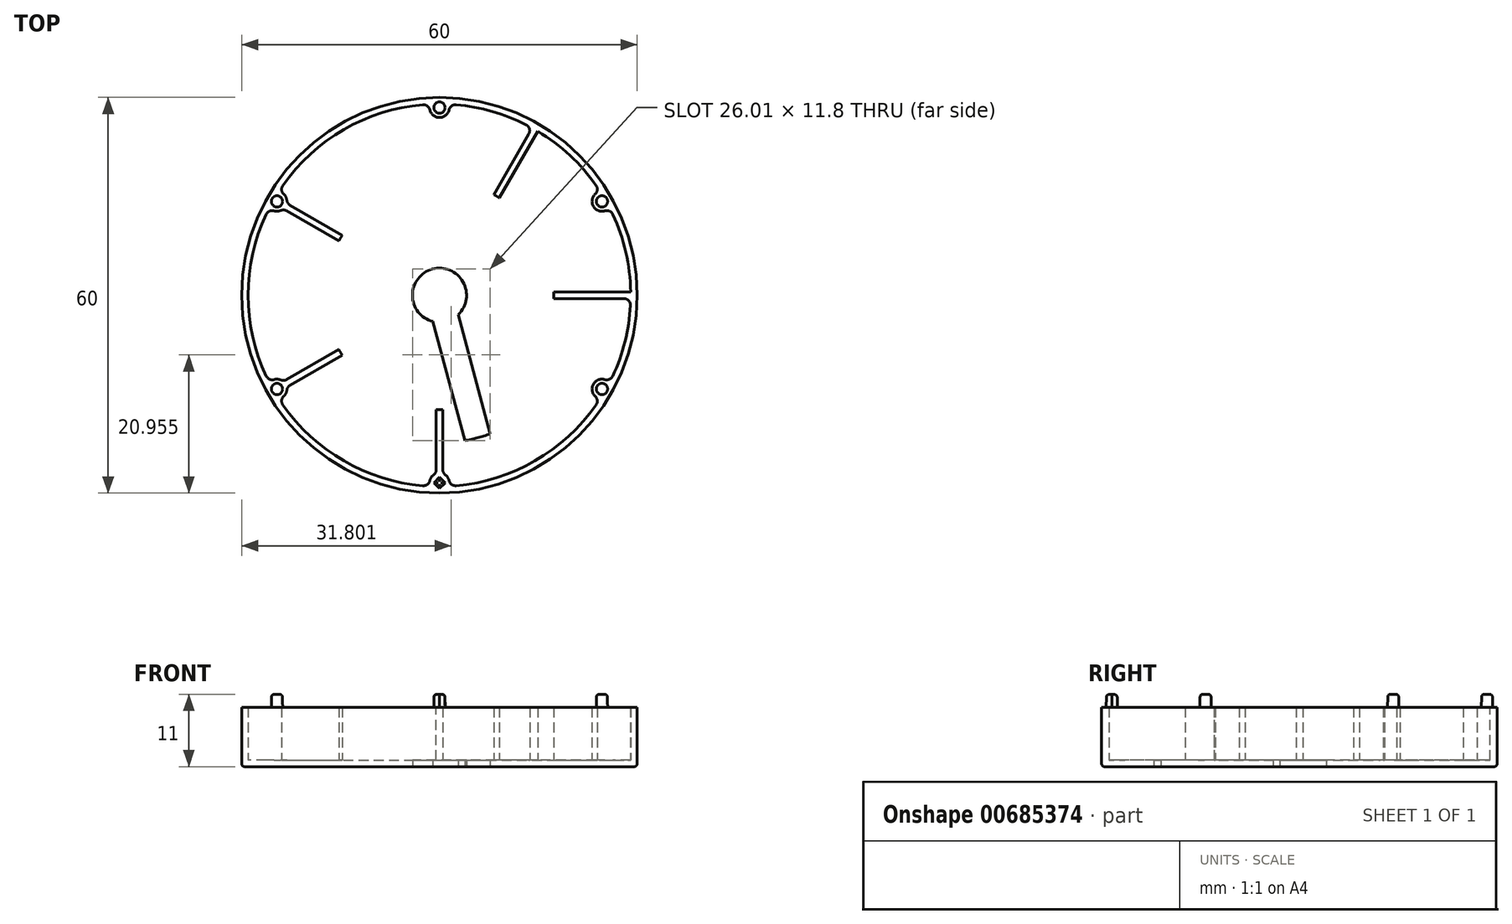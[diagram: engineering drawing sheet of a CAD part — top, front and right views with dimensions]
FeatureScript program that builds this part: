
annotation { "Feature Type Name" : "Feature", "Feature Type Description" : "" }
export const myFeature = defineFeature(function(context is Context, id is Id, definition is map)
    precondition{}
    {
        {
            var Q0;
            Q0=qCreatedBy(makeId("Top.planeOp"),FACE);
            var sketch = newSketch(context, id + "F0", { "sketchPlane" : qUnion([Q0])});
            skCircle(sketch, "E0", {"center": v(0, 0) * mm, "radius": 30 * mm});
            skCircle(sketch, "E1.0", {"center": v(0, 0) * mm, "radius": 29 * mm});
            skLineSegment(sketch, "E2.bottom", {"start": v(14.56, 26.23) * mm, "end": v(15.43, 25.73) * mm});
            skLineSegment(sketch, "E2.top", {"start": v(-15.43, -25.73) * mm, "end": v(-14.56, -26.23) * mm});
            skLineSegment(sketch, "E2.left", {"start": v(14.56, 26.23) * mm, "end": v(-15.43, -25.73) * mm});
            skLineSegment(sketch, "E2.right", {"start": v(15.43, 25.73) * mm, "end": v(-14.56, -26.23) * mm});
            skLineSegment(sketch, "E3.bottom", {"start": v(25.73, 15.43) * mm, "end": v(26.23, 14.56) * mm});
            skLineSegment(sketch, "E3.top", {"start": v(-26.23, -14.56) * mm, "end": v(-25.73, -15.43) * mm});
            skLineSegment(sketch, "E3.left", {"start": v(25.73, 15.43) * mm, "end": v(-26.23, -14.56) * mm});
            skLineSegment(sketch, "E3.right", {"start": v(26.23, 14.56) * mm, "end": v(-25.73, -15.43) * mm});
            skLineSegment(sketch, "E4", {"start": v(-38.35, 0) * mm, "end": v(39.17, 0) * mm, "construction": true});
            skLineSegment(sketch, "E5", {"start": v(0, 42.5) * mm, "end": v(0, -42.47) * mm, "construction": true});
            skLineSegment(sketch, "E6.bottom", {"start": v(-30, 0.5) * mm, "end": v(30, 0.5) * mm});
            skLineSegment(sketch, "E6.top", {"start": v(-30, -0.5) * mm, "end": v(30, -0.5) * mm});
            skLineSegment(sketch, "E6.left", {"start": v(-30, 0.5) * mm, "end": v(-30, -0.5) * mm});
            skLineSegment(sketch, "E6.right", {"start": v(30, 0.5) * mm, "end": v(30, -0.5) * mm});
            skLineSegment(sketch, "E7.bottom", {"start": v(-25.73, 15.43) * mm, "end": v(26.23, -14.56) * mm});
            skLineSegment(sketch, "E7.top", {"start": v(-26.23, 14.56) * mm, "end": v(25.73, -15.43) * mm});
            skLineSegment(sketch, "E7.left", {"start": v(-25.73, 15.43) * mm, "end": v(-26.23, 14.56) * mm});
            skLineSegment(sketch, "E7.right", {"start": v(26.23, -14.56) * mm, "end": v(25.73, -15.43) * mm});
            skLineSegment(sketch, "E8.bottom", {"start": v(-0.5, 30) * mm, "end": v(0.5, 30) * mm});
            skLineSegment(sketch, "E8.top", {"start": v(-0.5, -30) * mm, "end": v(0.5, -30) * mm});
            skLineSegment(sketch, "E8.left", {"start": v(-0.5, 30) * mm, "end": v(-0.5, -30) * mm});
            skLineSegment(sketch, "E8.right", {"start": v(0.5, 30) * mm, "end": v(0.5, -30) * mm});
            skLineSegment(sketch, "E9.bottom", {"start": v(-15.43, 25.73) * mm, "end": v(-14.56, 26.23) * mm});
            skLineSegment(sketch, "E9.top", {"start": v(14.56, -26.23) * mm, "end": v(15.43, -25.73) * mm});
            skLineSegment(sketch, "E9.left", {"start": v(-15.43, 25.73) * mm, "end": v(14.56, -26.23) * mm});
            skLineSegment(sketch, "E9.right", {"start": v(-14.56, 26.23) * mm, "end": v(15.43, -25.73) * mm});
            skCircle(sketch, "E10", {"center": v(0, 0) * mm, "radius": 17.33 * mm});
            skSolve(sketch);
        }
        {
            var Q0;
            Q0=qCreatedBy(makeId("Top.planeOp"),FACE);
            var sketch = newSketch(context, id + "F1", { "sketchPlane" : qUnion([Q0])});
            skCircle(sketch, "E11", {"center": v(0, 0) * mm, "radius": 30 * mm});
            skCircle(sketch, "E12", {"center": v(0, 0) * mm, "radius": 29 * mm});
            skSolve(sketch);
        }
        {
            var Q0;
            Q0=makeQuery(id+"F1.imprint","IMPRINT",FACE,{"disambiguationData":[TD([[makeQuery(id+"F1.imprint","IMPRINT",EDGE,{"derivedFrom":sQuery(id+"F1.wireOp",EDGE,"E11")}),1.0]])]});
            extrude(context, id + "F2", {"entities" : qUnion([Q0]), "depth" : 9 * mm, "offsetDistance" : 25 * mm});
        }
        {
            var Q0;
            Q0=qSketchRegion(id+"F1",true);
            var Q1;
            {var subQ0=sQuery(id+"F0.wireOp",EDGE,"E7.bottom");var subQ1=sQuery(id+"F0.wireOp",EDGE,"E1.0");var subQ2=makeQuery(id+"F0.imprint","INTERSECT",VERTEX,{"disambiguationData":[OD(0.0)],"derivedFrom":[subQ1,subQ0]});Q1=makeQuery(id+"F0.imprint","IMPRINT",FACE,{"disambiguationData":[TD([[makeQuery(id+"F0.imprint","IMPRINT",EDGE,{"disambiguationData":[TD([[subQ2,-1.0]])],"derivedFrom":subQ1}),1.0]])]});}
            var Q2;
            {var subQ0=sQuery(id+"F0.wireOp",EDGE,"E2.right");var subQ1=sQuery(id+"F0.wireOp",EDGE,"E1.0");var subQ2=makeQuery(id+"F0.imprint","INTERSECT",VERTEX,{"disambiguationData":[OD(0.0)],"derivedFrom":[subQ1,subQ0]});Q2=makeQuery(id+"F0.imprint","IMPRINT",FACE,{"disambiguationData":[TD([[makeQuery(id+"F0.imprint","IMPRINT",EDGE,{"disambiguationData":[TD([[subQ2,-1.0]])],"derivedFrom":subQ1}),1.0]])]});}
            var Q3;
            {var subQ0=sQuery(id+"F0.wireOp",EDGE,"E6.bottom");var subQ1=sQuery(id+"F0.wireOp",EDGE,"E1.0");var subQ2=makeQuery(id+"F0.imprint","INTERSECT",VERTEX,{"disambiguationData":[OD(0.0)],"derivedFrom":[subQ1,subQ0]});Q3=makeQuery(id+"F0.imprint","IMPRINT",FACE,{"disambiguationData":[TD([[makeQuery(id+"F0.imprint","IMPRINT",EDGE,{"disambiguationData":[TD([[subQ2,1.0]])],"derivedFrom":subQ1}),1.0]])]});}
            var Q4;
            {var subQ0=sQuery(id+"F0.wireOp",EDGE,"E8.left");var subQ1=sQuery(id+"F0.wireOp",EDGE,"E1.0");var subQ2=makeQuery(id+"F0.imprint","INTERSECT",VERTEX,{"disambiguationData":[OD(1.0)],"derivedFrom":[subQ1,subQ0]});Q4=makeQuery(id+"F0.imprint","IMPRINT",FACE,{"disambiguationData":[TD([[makeQuery(id+"F0.imprint","IMPRINT",EDGE,{"disambiguationData":[TD([[subQ2,-1.0]])],"derivedFrom":subQ1}),1.0]])]});}
            var Q5;
            {var subQ0=sQuery(id+"F0.wireOp",EDGE,"E3.left");var subQ1=sQuery(id+"F0.wireOp",EDGE,"E1.0");var subQ2=makeQuery(id+"F0.imprint","INTERSECT",VERTEX,{"disambiguationData":[OD(1.0)],"derivedFrom":[subQ1,subQ0]});Q5=makeQuery(id+"F0.imprint","IMPRINT",FACE,{"disambiguationData":[TD([[makeQuery(id+"F0.imprint","IMPRINT",EDGE,{"disambiguationData":[TD([[subQ2,-1.0]])],"derivedFrom":subQ1}),1.0]])]});}
            extrude(context, id + "F3", {"entities" : qUnion([Q0, Q1, Q2, Q3, Q4, Q5]), "operationType" : NewBodyOperationType.ADD, "depth" : 9 * mm, "offsetDistance" : 25 * mm});
        }
        {
            var Q0;
            Q0=makeQuery(id+"F1.imprint","IMPRINT",FACE,{"disambiguationData":[TD([[makeQuery(id+"F1.imprint","IMPRINT",EDGE,{"derivedFrom":sQuery(id+"F1.wireOp",EDGE,"E11")}),1.0]])]});
            var Q1;
            Q1=makeQuery(id+"F1.imprint","IMPRINT",FACE,{"disambiguationData":[TD([[makeQuery(id+"F1.imprint","IMPRINT",EDGE,{"derivedFrom":sQuery(id+"F1.wireOp",EDGE,"E12")}),1.0]])]});
            extrude(context, id + "F4", {"entities" : qUnion([Q0, Q1]), "operationType" : NewBodyOperationType.ADD, "depth" : 1 * mm, "offsetDistance" : 25 * mm});
        }
        {
            var Q0;
            Q0=qCreatedBy(makeId("Top.planeOp"),FACE);
            var sketch = newSketch(context, id + "F5", { "sketchPlane" : qUnion([Q0])});
            skCircle(sketch, "E13", {"center": v(0, 0) * mm, "radius": 28.45 * mm});
            skLineSegment(sketch, "E14", {"start": v(0, 28.45) * mm, "end": v(0, -28.45) * mm, "construction": true});
            skLineSegment(sketch, "E15", {"start": v(24.64, 14.22) * mm, "end": v(0, 0) * mm, "construction": true});
            skLineSegment(sketch, "E16", {"start": v(14.23, 24.64) * mm, "end": v(0, 0) * mm, "construction": true});
            skLineSegment(sketch, "E17", {"start": v(0, 0) * mm, "end": v(28.45, 0) * mm, "construction": true});
            skLineSegment(sketch, "E18", {"start": v(0, 0) * mm, "end": v(24.64, -14.22) * mm, "construction": true});
            skLineSegment(sketch, "E19", {"start": v(0, 0) * mm, "end": v(14.23, -24.64) * mm, "construction": true});
            skLineSegment(sketch, "E20", {"start": v(0, 0) * mm, "end": v(-14.23, 24.64) * mm, "construction": true});
            skLineSegment(sketch, "E21", {"start": v(0, 0) * mm, "end": v(-24.64, 14.22) * mm, "construction": true});
            skLineSegment(sketch, "E22", {"start": v(0, 0) * mm, "end": v(-28.45, 0) * mm, "construction": true});
            skLineSegment(sketch, "E23", {"start": v(0, 0) * mm, "end": v(-24.64, -14.23) * mm, "construction": true});
            skLineSegment(sketch, "E24", {"start": v(0, 0) * mm, "end": v(-14.22, -24.64) * mm, "construction": true});
            skCircle(sketch, "E25", {"center": v(0, 28.45) * mm, "radius": 1.5 * mm});
            skCircle(sketch, "E26", {"center": v(24.64, 14.22) * mm, "radius": 1.5 * mm});
            skCircle(sketch, "E27", {"center": v(24.64, -14.22) * mm, "radius": 1.5 * mm});
            skCircle(sketch, "E28", {"center": v(0, -28.45) * mm, "radius": 1.5 * mm});
            skCircle(sketch, "E29", {"center": v(-24.64, -14.23) * mm, "radius": 1.5 * mm});
            skCircle(sketch, "E30", {"center": v(-24.64, 14.22) * mm, "radius": 1.5 * mm});
            skCircle(sketch, "E31", {"center": v(-24.64, 14.22) * mm, "radius": 1 * mm});
            skCircle(sketch, "E32", {"center": v(0, 28.45) * mm, "radius": 1 * mm});
            skCircle(sketch, "E33", {"center": v(24.64, 14.22) * mm, "radius": 1 * mm});
            skCircle(sketch, "E34", {"center": v(24.64, -14.22) * mm, "radius": 1 * mm});
            skCircle(sketch, "E35", {"center": v(-24.64, -14.23) * mm, "radius": 1 * mm});
            skLineSegment(sketch, "E36.bottom", {"start": v(1.06, -28.45) * mm, "end": v(0, -29.51) * mm});
            skLineSegment(sketch, "E36.top", {"start": v(0, -27.39) * mm, "end": v(-1.06, -28.45) * mm});
            skLineSegment(sketch, "E36.left", {"start": v(1.06, -28.45) * mm, "end": v(0, -27.39) * mm});
            skLineSegment(sketch, "E36.right", {"start": v(0, -29.51) * mm, "end": v(-1.06, -28.45) * mm});
            skSolve(sketch);
        }
        {
            var Q0;
            {var subQ0=sQuery(id+"F5.wireOp",EDGE,"E30");var subQ1=sQuery(id+"F5.wireOp",EDGE,"E13");var subQ2=makeQuery(id+"F5.imprint","INTERSECT",VERTEX,{"disambiguationData":[OD(0.0)],"derivedFrom":[subQ1,subQ0]});Q0=makeQuery(id+"F5.imprint","IMPRINT",FACE,{"disambiguationData":[TD([[makeQuery(id+"F5.imprint","IMPRINT",EDGE,{"disambiguationData":[TD([[subQ2,-1.0]])],"derivedFrom":subQ1}),1.0]])]});}
            var Q1;
            {var subQ0=sQuery(id+"F5.wireOp",EDGE,"E30");var subQ1=sQuery(id+"F5.wireOp",EDGE,"E13");var subQ2=makeQuery(id+"F5.imprint","INTERSECT",VERTEX,{"disambiguationData":[OD(0.0)],"derivedFrom":[subQ1,subQ0]});Q1=makeQuery(id+"F5.imprint","IMPRINT",FACE,{"disambiguationData":[TD([[makeQuery(id+"F5.imprint","IMPRINT",EDGE,{"disambiguationData":[TD([[subQ2,-1.0]])],"derivedFrom":subQ1}),-1.0]])]});}
            var Q2;
            {var subQ0=sQuery(id+"F5.wireOp",EDGE,"E25");var subQ1=sQuery(id+"F5.wireOp",EDGE,"E13");var subQ2=makeQuery(id+"F5.imprint","INTERSECT",VERTEX,{"disambiguationData":[OD(0.0)],"derivedFrom":[subQ1,subQ0]});Q2=makeQuery(id+"F5.imprint","IMPRINT",FACE,{"disambiguationData":[TD([[makeQuery(id+"F5.imprint","IMPRINT",EDGE,{"disambiguationData":[TD([[subQ2,-1.0]])],"derivedFrom":subQ1}),1.0]])]});}
            var Q3;
            {var subQ0=sQuery(id+"F5.wireOp",EDGE,"E25");var subQ1=sQuery(id+"F5.wireOp",EDGE,"E13");var subQ2=makeQuery(id+"F5.imprint","INTERSECT",VERTEX,{"disambiguationData":[OD(0.0)],"derivedFrom":[subQ1,subQ0]});Q3=makeQuery(id+"F5.imprint","IMPRINT",FACE,{"disambiguationData":[TD([[makeQuery(id+"F5.imprint","IMPRINT",EDGE,{"disambiguationData":[TD([[subQ2,-1.0]])],"derivedFrom":subQ1}),-1.0]])]});}
            var Q4;
            {var subQ0=sQuery(id+"F5.wireOp",EDGE,"E26");var subQ1=sQuery(id+"F5.wireOp",EDGE,"E13");var subQ2=makeQuery(id+"F5.imprint","INTERSECT",VERTEX,{"disambiguationData":[OD(0.0)],"derivedFrom":[subQ1,subQ0]});Q4=makeQuery(id+"F5.imprint","IMPRINT",FACE,{"disambiguationData":[TD([[makeQuery(id+"F5.imprint","IMPRINT",EDGE,{"disambiguationData":[TD([[subQ2,-1.0]])],"derivedFrom":subQ1}),-1.0]])]});}
            var Q5;
            {var subQ0=sQuery(id+"F5.wireOp",EDGE,"E26");var subQ1=sQuery(id+"F5.wireOp",EDGE,"E13");var subQ2=makeQuery(id+"F5.imprint","INTERSECT",VERTEX,{"disambiguationData":[OD(0.0)],"derivedFrom":[subQ1,subQ0]});Q5=makeQuery(id+"F5.imprint","IMPRINT",FACE,{"disambiguationData":[TD([[makeQuery(id+"F5.imprint","IMPRINT",EDGE,{"disambiguationData":[TD([[subQ2,-1.0]])],"derivedFrom":subQ1}),1.0]])]});}
            var Q6;
            {var subQ0=sQuery(id+"F5.wireOp",EDGE,"E29");var subQ1=sQuery(id+"F5.wireOp",EDGE,"E13");var subQ2=makeQuery(id+"F5.imprint","INTERSECT",VERTEX,{"disambiguationData":[OD(0.0)],"derivedFrom":[subQ1,subQ0]});Q6=makeQuery(id+"F5.imprint","IMPRINT",FACE,{"disambiguationData":[TD([[makeQuery(id+"F5.imprint","IMPRINT",EDGE,{"disambiguationData":[TD([[subQ2,-1.0]])],"derivedFrom":subQ1}),1.0]])]});}
            var Q7;
            {var subQ0=sQuery(id+"F5.wireOp",EDGE,"E29");var subQ1=sQuery(id+"F5.wireOp",EDGE,"E13");var subQ2=makeQuery(id+"F5.imprint","INTERSECT",VERTEX,{"disambiguationData":[OD(0.0)],"derivedFrom":[subQ1,subQ0]});Q7=makeQuery(id+"F5.imprint","IMPRINT",FACE,{"disambiguationData":[TD([[makeQuery(id+"F5.imprint","IMPRINT",EDGE,{"disambiguationData":[TD([[subQ2,-1.0]])],"derivedFrom":subQ1}),-1.0]])]});}
            var Q8;
            {var subQ3=sQuery(id+"F5.wireOp",EDGE,"E13");var subQ5=sQuery(id+"F5.wireOp",EDGE,"E28");var subQ6=makeQuery(id+"F5.imprint","INTERSECT",VERTEX,{"disambiguationData":[OD(0.0)],"derivedFrom":[subQ3,subQ5]});Q8=makeQuery(id+"F5.imprint","IMPRINT",FACE,{"disambiguationData":[TD([[makeQuery(id+"F5.imprint","IMPRINT",EDGE,{"disambiguationData":[TD([[subQ6,-1.0]])],"derivedFrom":subQ3}),1.0]])]});}
            var Q9;
            {var subQ6=sQuery(id+"F5.wireOp",EDGE,"E36.bottom");Q9=makeQuery(id+"F5.imprint","IMPRINT",FACE,{"disambiguationData":[TD([[makeQuery(id+"F5.imprint","IMPRINT",EDGE,{"derivedFrom":subQ6}),1.0]])]});}
            var Q10;
            {var subQ0=sQuery(id+"F5.wireOp",EDGE,"E27");var subQ1=sQuery(id+"F5.wireOp",EDGE,"E13");var subQ2=makeQuery(id+"F5.imprint","INTERSECT",VERTEX,{"disambiguationData":[OD(0.0)],"derivedFrom":[subQ1,subQ0]});Q10=makeQuery(id+"F5.imprint","IMPRINT",FACE,{"disambiguationData":[TD([[makeQuery(id+"F5.imprint","IMPRINT",EDGE,{"disambiguationData":[TD([[subQ2,-1.0]])],"derivedFrom":subQ1}),-1.0]])]});}
            var Q11;
            {var subQ0=sQuery(id+"F5.wireOp",EDGE,"E27");var subQ1=sQuery(id+"F5.wireOp",EDGE,"E13");var subQ2=makeQuery(id+"F5.imprint","INTERSECT",VERTEX,{"disambiguationData":[OD(0.0)],"derivedFrom":[subQ1,subQ0]});Q11=makeQuery(id+"F5.imprint","IMPRINT",FACE,{"disambiguationData":[TD([[makeQuery(id+"F5.imprint","IMPRINT",EDGE,{"disambiguationData":[TD([[subQ2,-1.0]])],"derivedFrom":subQ1}),1.0]])]});}
            var Q12;
            {var subQ0=sQuery(id+"F5.wireOp",EDGE,"E31");var subQ1=sQuery(id+"F5.wireOp",EDGE,"E13");var subQ2=makeQuery(id+"F5.imprint","INTERSECT",VERTEX,{"disambiguationData":[OD(0.0)],"derivedFrom":[subQ1,subQ0]});Q12=makeQuery(id+"F5.imprint","IMPRINT",FACE,{"disambiguationData":[TD([[makeQuery(id+"F5.imprint","IMPRINT",EDGE,{"disambiguationData":[TD([[subQ2,-1.0]])],"derivedFrom":subQ1}),1.0]])]});}
            var Q13;
            {var subQ0=sQuery(id+"F5.wireOp",EDGE,"E31");var subQ1=sQuery(id+"F5.wireOp",EDGE,"E13");var subQ2=makeQuery(id+"F5.imprint","INTERSECT",VERTEX,{"disambiguationData":[OD(0.0)],"derivedFrom":[subQ1,subQ0]});Q13=makeQuery(id+"F5.imprint","IMPRINT",FACE,{"disambiguationData":[TD([[makeQuery(id+"F5.imprint","IMPRINT",EDGE,{"disambiguationData":[TD([[subQ2,-1.0]])],"derivedFrom":subQ1}),-1.0]])]});}
            var Q14;
            {var subQ0=sQuery(id+"F5.wireOp",EDGE,"E32");var subQ1=sQuery(id+"F5.wireOp",EDGE,"E13");var subQ2=makeQuery(id+"F5.imprint","INTERSECT",VERTEX,{"disambiguationData":[OD(0.0)],"derivedFrom":[subQ1,subQ0]});Q14=makeQuery(id+"F5.imprint","IMPRINT",FACE,{"disambiguationData":[TD([[makeQuery(id+"F5.imprint","IMPRINT",EDGE,{"disambiguationData":[TD([[subQ2,-1.0]])],"derivedFrom":subQ1}),-1.0]])]});}
            var Q15;
            {var subQ0=sQuery(id+"F5.wireOp",EDGE,"E32");var subQ1=sQuery(id+"F5.wireOp",EDGE,"E13");var subQ2=makeQuery(id+"F5.imprint","INTERSECT",VERTEX,{"disambiguationData":[OD(0.0)],"derivedFrom":[subQ1,subQ0]});Q15=makeQuery(id+"F5.imprint","IMPRINT",FACE,{"disambiguationData":[TD([[makeQuery(id+"F5.imprint","IMPRINT",EDGE,{"disambiguationData":[TD([[subQ2,-1.0]])],"derivedFrom":subQ1}),1.0]])]});}
            var Q16;
            {var subQ0=sQuery(id+"F5.wireOp",EDGE,"E33");var subQ1=sQuery(id+"F5.wireOp",EDGE,"E13");var subQ2=makeQuery(id+"F5.imprint","INTERSECT",VERTEX,{"disambiguationData":[OD(0.0)],"derivedFrom":[subQ1,subQ0]});Q16=makeQuery(id+"F5.imprint","IMPRINT",FACE,{"disambiguationData":[TD([[makeQuery(id+"F5.imprint","IMPRINT",EDGE,{"disambiguationData":[TD([[subQ2,-1.0]])],"derivedFrom":subQ1}),-1.0]])]});}
            var Q17;
            {var subQ0=sQuery(id+"F5.wireOp",EDGE,"E33");var subQ1=sQuery(id+"F5.wireOp",EDGE,"E13");var subQ2=makeQuery(id+"F5.imprint","INTERSECT",VERTEX,{"disambiguationData":[OD(0.0)],"derivedFrom":[subQ1,subQ0]});Q17=makeQuery(id+"F5.imprint","IMPRINT",FACE,{"disambiguationData":[TD([[makeQuery(id+"F5.imprint","IMPRINT",EDGE,{"disambiguationData":[TD([[subQ2,-1.0]])],"derivedFrom":subQ1}),1.0]])]});}
            var Q18;
            {var subQ0=sQuery(id+"F5.wireOp",EDGE,"E34");var subQ1=sQuery(id+"F5.wireOp",EDGE,"E13");var subQ2=makeQuery(id+"F5.imprint","INTERSECT",VERTEX,{"disambiguationData":[OD(0.0)],"derivedFrom":[subQ1,subQ0]});Q18=makeQuery(id+"F5.imprint","IMPRINT",FACE,{"disambiguationData":[TD([[makeQuery(id+"F5.imprint","IMPRINT",EDGE,{"disambiguationData":[TD([[subQ2,-1.0]])],"derivedFrom":subQ1}),-1.0]])]});}
            var Q19;
            {var subQ0=sQuery(id+"F5.wireOp",EDGE,"E34");var subQ1=sQuery(id+"F5.wireOp",EDGE,"E13");var subQ2=makeQuery(id+"F5.imprint","INTERSECT",VERTEX,{"disambiguationData":[OD(0.0)],"derivedFrom":[subQ1,subQ0]});Q19=makeQuery(id+"F5.imprint","IMPRINT",FACE,{"disambiguationData":[TD([[makeQuery(id+"F5.imprint","IMPRINT",EDGE,{"disambiguationData":[TD([[subQ2,-1.0]])],"derivedFrom":subQ1}),1.0]])]});}
            var Q20;
            {var subQ1=sQuery(id+"F5.wireOp",EDGE,"E36.bottom");Q20=makeQuery(id+"F5.imprint","IMPRINT",FACE,{"disambiguationData":[TD([[makeQuery(id+"F5.imprint","IMPRINT",EDGE,{"derivedFrom":subQ1}),-1.0]])]});}
            var Q21;
            {var subQ0=sQuery(id+"F5.wireOp",EDGE,"E35");var subQ1=sQuery(id+"F5.wireOp",EDGE,"E13");var subQ2=makeQuery(id+"F5.imprint","INTERSECT",VERTEX,{"disambiguationData":[OD(0.0)],"derivedFrom":[subQ1,subQ0]});Q21=makeQuery(id+"F5.imprint","IMPRINT",FACE,{"disambiguationData":[TD([[makeQuery(id+"F5.imprint","IMPRINT",EDGE,{"disambiguationData":[TD([[subQ2,-1.0]])],"derivedFrom":subQ1}),-1.0]])]});}
            var Q22;
            {var subQ0=sQuery(id+"F5.wireOp",EDGE,"E35");var subQ1=sQuery(id+"F5.wireOp",EDGE,"E13");var subQ2=makeQuery(id+"F5.imprint","INTERSECT",VERTEX,{"disambiguationData":[OD(0.0)],"derivedFrom":[subQ1,subQ0]});Q22=makeQuery(id+"F5.imprint","IMPRINT",FACE,{"disambiguationData":[TD([[makeQuery(id+"F5.imprint","IMPRINT",EDGE,{"disambiguationData":[TD([[subQ2,-1.0]])],"derivedFrom":subQ1}),1.0]])]});}
            var Q23;
            {var subQ0=sQuery(id+"F5.wireOp",EDGE,"E36.top");var subQ1=sQuery(id+"F5.wireOp",EDGE,"E13");var subQ2=makeQuery(id+"F5.imprint","INTERSECT",VERTEX,{"derivedFrom":[subQ1,subQ0]});Q23=makeQuery(id+"F5.imprint","IMPRINT",FACE,{"disambiguationData":[TD([[makeQuery(id+"F5.imprint","IMPRINT",EDGE,{"disambiguationData":[TD([[subQ2,-1.0]])],"derivedFrom":subQ1}),1.0]])]});}
            extrude(context, id + "F6", {"entities" : qUnion([Q0, Q1, Q2, Q3, Q4, Q5, Q6, Q7, Q8, Q9, Q10, Q11, Q12, Q13, Q14, Q15, Q16, Q17, Q18, Q19, Q20, Q21, Q22, Q23]), "operationType" : NewBodyOperationType.ADD, "depth" : 9 * mm, "offsetDistance" : 25 * mm});
        }
        {
            var Q0;
            {var subQ0=sQuery(id+"F0.wireOp",EDGE,"E8.right");var subQ1=sQuery(id+"F0.wireOp",EDGE,"E1.0");Q0=makeQuery(id+"F3.opExtrude","SWEPT_EDGE",EDGE,{"disambiguationData":[OSD([subQ1,subQ0]),TDD([makeQuery(id+"F0.imprint","INTERSECT",VERTEX,{"disambiguationData":[OD(1.0)],"derivedFrom":[subQ1,subQ0]})])]});}
            var Q1;
            {var subQ0=sQuery(id+"F0.wireOp",EDGE,"E2.left");var subQ1=sQuery(id+"F0.wireOp",EDGE,"E1.0");Q1=makeQuery(id+"F3.opExtrude","SWEPT_EDGE",EDGE,{"disambiguationData":[OSD([subQ1,subQ0]),TDD([makeQuery(id+"F0.imprint","INTERSECT",VERTEX,{"disambiguationData":[OD(1.0)],"derivedFrom":[subQ1,subQ0]})])]});}
            var Q2;
            {var subQ0=sQuery(id+"F0.wireOp",EDGE,"E3.left");var subQ1=sQuery(id+"F0.wireOp",EDGE,"E1.0");Q2=makeQuery(id+"F3.opExtrude","SWEPT_EDGE",EDGE,{"disambiguationData":[OSD([subQ1,subQ0]),TDD([makeQuery(id+"F0.imprint","INTERSECT",VERTEX,{"disambiguationData":[OD(1.0)],"derivedFrom":[subQ1,subQ0]})])]});}
            var Q3;
            {var subQ0=sQuery(id+"F0.wireOp",EDGE,"E6.bottom");var subQ1=sQuery(id+"F0.wireOp",EDGE,"E1.0");Q3=makeQuery(id+"F3.opExtrude","SWEPT_EDGE",EDGE,{"disambiguationData":[OSD([subQ1,subQ0]),TDD([makeQuery(id+"F0.imprint","INTERSECT",VERTEX,{"disambiguationData":[OD(1.0)],"derivedFrom":[subQ1,subQ0]})])]});}
            var Q4;
            {var subQ0=sQuery(id+"F0.wireOp",EDGE,"E9.right");var subQ1=sQuery(id+"F0.wireOp",EDGE,"E1.0");Q4=makeQuery(id+"F3.opExtrude","SWEPT_EDGE",EDGE,{"disambiguationData":[OSD([subQ1,subQ0]),TDD([makeQuery(id+"F0.imprint","INTERSECT",VERTEX,{"disambiguationData":[OD(1.0)],"derivedFrom":[subQ1,subQ0]})])]});}
            var Q5;
            {var subQ0=sQuery(id+"F0.wireOp",EDGE,"E7.bottom");var subQ1=sQuery(id+"F0.wireOp",EDGE,"E1.0");Q5=makeQuery(id+"F3.opExtrude","SWEPT_EDGE",EDGE,{"disambiguationData":[OSD([subQ1,subQ0]),TDD([makeQuery(id+"F0.imprint","INTERSECT",VERTEX,{"disambiguationData":[OD(1.0)],"derivedFrom":[subQ1,subQ0]})])]});}
            var Q6;
            {var subQ0=sQuery(id+"F0.wireOp",EDGE,"E8.left");var subQ1=sQuery(id+"F0.wireOp",EDGE,"E1.0");Q6=makeQuery(id+"F3.opExtrude","SWEPT_EDGE",EDGE,{"disambiguationData":[OSD([subQ1,subQ0]),TDD([makeQuery(id+"F0.imprint","INTERSECT",VERTEX,{"disambiguationData":[OD(0.0)],"derivedFrom":[subQ1,subQ0]})])]});}
            var Q7;
            {var subQ0=sQuery(id+"F0.wireOp",EDGE,"E2.left");var subQ1=sQuery(id+"F0.wireOp",EDGE,"E1.0");Q7=makeQuery(id+"F3.opExtrude","SWEPT_EDGE",EDGE,{"disambiguationData":[OSD([subQ1,subQ0]),TDD([makeQuery(id+"F0.imprint","INTERSECT",VERTEX,{"disambiguationData":[OD(0.0)],"derivedFrom":[subQ1,subQ0]})])]});}
            var Q8;
            {var subQ0=sQuery(id+"F0.wireOp",EDGE,"E3.left");var subQ1=sQuery(id+"F0.wireOp",EDGE,"E1.0");Q8=makeQuery(id+"F3.opExtrude","SWEPT_EDGE",EDGE,{"disambiguationData":[OSD([subQ1,subQ0]),TDD([makeQuery(id+"F0.imprint","INTERSECT",VERTEX,{"disambiguationData":[OD(0.0)],"derivedFrom":[subQ1,subQ0]})])]});}
            var Q9;
            {var subQ0=sQuery(id+"F0.wireOp",EDGE,"E6.top");var subQ1=sQuery(id+"F0.wireOp",EDGE,"E1.0");Q9=makeQuery(id+"F3.opExtrude","SWEPT_EDGE",EDGE,{"disambiguationData":[OSD([subQ1,subQ0]),TDD([makeQuery(id+"F0.imprint","INTERSECT",VERTEX,{"disambiguationData":[OD(1.0)],"derivedFrom":[subQ1,subQ0]})])]});}
            var Q10;
            {var subQ0=sQuery(id+"F0.wireOp",EDGE,"E7.top");var subQ1=sQuery(id+"F0.wireOp",EDGE,"E1.0");Q10=makeQuery(id+"F3.opExtrude","SWEPT_EDGE",EDGE,{"disambiguationData":[OSD([subQ1,subQ0]),TDD([makeQuery(id+"F0.imprint","INTERSECT",VERTEX,{"disambiguationData":[OD(0.0)],"derivedFrom":[subQ1,subQ0]})])]});}
            var Q11;
            {var subQ0=sQuery(id+"F0.wireOp",EDGE,"E6.top");var subQ1=sQuery(id+"F0.wireOp",EDGE,"E1.0");Q11=makeQuery(id+"F3.opExtrude","SWEPT_EDGE",EDGE,{"disambiguationData":[OSD([subQ1,subQ0]),TDD([makeQuery(id+"F0.imprint","INTERSECT",VERTEX,{"disambiguationData":[OD(0.0)],"derivedFrom":[subQ1,subQ0]})])]});}
            var Q12;
            {var subQ0=sQuery(id+"F0.wireOp",EDGE,"E9.left");var subQ1=sQuery(id+"F0.wireOp",EDGE,"E1.0");Q12=makeQuery(id+"F3.opExtrude","SWEPT_EDGE",EDGE,{"disambiguationData":[OSD([subQ1,subQ0]),TDD([makeQuery(id+"F0.imprint","INTERSECT",VERTEX,{"disambiguationData":[OD(0.0)],"derivedFrom":[subQ1,subQ0]})])]});}
            var Q13;
            {var subQ0=sQuery(id+"F0.wireOp",EDGE,"E8.right");var subQ1=sQuery(id+"F0.wireOp",EDGE,"E1.0");Q13=makeQuery(id+"F3.opExtrude","SWEPT_EDGE",EDGE,{"disambiguationData":[OSD([subQ1,subQ0]),TDD([makeQuery(id+"F0.imprint","INTERSECT",VERTEX,{"disambiguationData":[OD(0.0)],"derivedFrom":[subQ1,subQ0]})])]});}
            var Q14;
            {var subQ0=sQuery(id+"F0.wireOp",EDGE,"E7.bottom");var subQ1=sQuery(id+"F0.wireOp",EDGE,"E1.0");Q14=makeQuery(id+"F3.opExtrude","SWEPT_EDGE",EDGE,{"disambiguationData":[OSD([subQ1,subQ0]),TDD([makeQuery(id+"F0.imprint","INTERSECT",VERTEX,{"disambiguationData":[OD(0.0)],"derivedFrom":[subQ1,subQ0]})])]});}
            var Q15;
            {var subQ0=sQuery(id+"F0.wireOp",EDGE,"E9.right");var subQ1=sQuery(id+"F0.wireOp",EDGE,"E1.0");Q15=makeQuery(id+"F3.opExtrude","SWEPT_EDGE",EDGE,{"disambiguationData":[OSD([subQ1,subQ0]),TDD([makeQuery(id+"F0.imprint","INTERSECT",VERTEX,{"disambiguationData":[OD(0.0)],"derivedFrom":[subQ1,subQ0]})])]});}
            var Q16;
            {var subQ0=sQuery(id+"F0.wireOp",EDGE,"E3.right");var subQ1=sQuery(id+"F0.wireOp",EDGE,"E1.0");Q16=makeQuery(id+"F3.opExtrude","SWEPT_EDGE",EDGE,{"disambiguationData":[OSD([subQ1,subQ0]),TDD([makeQuery(id+"F0.imprint","INTERSECT",VERTEX,{"disambiguationData":[OD(1.0)],"derivedFrom":[subQ1,subQ0]})])]});}
            var Q17;
            {var subQ0=sQuery(id+"F0.wireOp",EDGE,"E2.right");var subQ1=sQuery(id+"F0.wireOp",EDGE,"E1.0");Q17=makeQuery(id+"F3.opExtrude","SWEPT_EDGE",EDGE,{"disambiguationData":[OSD([subQ1,subQ0]),TDD([makeQuery(id+"F0.imprint","INTERSECT",VERTEX,{"disambiguationData":[OD(1.0)],"derivedFrom":[subQ1,subQ0]})])]});}
            var Q18;
            {var subQ0=sQuery(id+"F0.wireOp",EDGE,"E3.right");var subQ1=sQuery(id+"F0.wireOp",EDGE,"E1.0");Q18=makeQuery(id+"F3.opExtrude","SWEPT_EDGE",EDGE,{"disambiguationData":[OSD([subQ1,subQ0]),TDD([makeQuery(id+"F0.imprint","INTERSECT",VERTEX,{"disambiguationData":[OD(0.0)],"derivedFrom":[subQ1,subQ0]})])]});}
            var Q19;
            {var subQ0=sQuery(id+"F0.wireOp",EDGE,"E2.right");var subQ1=sQuery(id+"F0.wireOp",EDGE,"E1.0");Q19=makeQuery(id+"F3.opExtrude","SWEPT_EDGE",EDGE,{"disambiguationData":[OSD([subQ1,subQ0]),TDD([makeQuery(id+"F0.imprint","INTERSECT",VERTEX,{"disambiguationData":[OD(0.0)],"derivedFrom":[subQ1,subQ0]})])]});}
            var Q20;
            {var subQ0=sQuery(id+"F0.wireOp",EDGE,"E8.left");var subQ1=sQuery(id+"F0.wireOp",EDGE,"E1.0");Q20=makeQuery(id+"F3.opExtrude","SWEPT_EDGE",EDGE,{"disambiguationData":[OSD([subQ1,subQ0]),TDD([makeQuery(id+"F0.imprint","INTERSECT",VERTEX,{"disambiguationData":[OD(1.0)],"derivedFrom":[subQ1,subQ0]})])]});}
            var Q21;
            {var subQ0=sQuery(id+"F0.wireOp",EDGE,"E9.left");var subQ1=sQuery(id+"F0.wireOp",EDGE,"E1.0");Q21=makeQuery(id+"F3.opExtrude","SWEPT_EDGE",EDGE,{"disambiguationData":[OSD([subQ1,subQ0]),TDD([makeQuery(id+"F0.imprint","INTERSECT",VERTEX,{"disambiguationData":[OD(1.0)],"derivedFrom":[subQ1,subQ0]})])]});}
            var Q22;
            {var subQ0=sQuery(id+"F0.wireOp",EDGE,"E7.top");var subQ1=sQuery(id+"F0.wireOp",EDGE,"E1.0");Q22=makeQuery(id+"F3.opExtrude","SWEPT_EDGE",EDGE,{"disambiguationData":[OSD([subQ1,subQ0]),TDD([makeQuery(id+"F0.imprint","INTERSECT",VERTEX,{"disambiguationData":[OD(1.0)],"derivedFrom":[subQ1,subQ0]})])]});}
            var Q23;
            {var subQ0=sQuery(id+"F0.wireOp",EDGE,"E6.bottom");var subQ1=sQuery(id+"F0.wireOp",EDGE,"E1.0");Q23=makeQuery(id+"F3.opExtrude","SWEPT_EDGE",EDGE,{"disambiguationData":[OSD([subQ1,subQ0]),TDD([makeQuery(id+"F0.imprint","INTERSECT",VERTEX,{"disambiguationData":[OD(0.0)],"derivedFrom":[subQ1,subQ0]})])]});}
            var Q24;
            {var subQ5=sQuery(id+"F0.wireOp",EDGE,"E3.left");var subQ8=sQuery(id+"F1.wireOp",EDGE,"E12");Q24=makeQuery(id+"F6.boolean.opBoolean","INTERSECT",EDGE,{"derivedFrom":[makeQuery(id+"F3.boolean.opBoolean","SPLIT",FACE,{"disambiguationData":[TD([makeQuery(id+"F3.opExtrude","SWEPT_FACE",FACE,{"disambiguationData":[OSD([subQ5])]})])],"derivedFrom":makeQuery(id+"F2.opExtrude","SWEPT_FACE",FACE,{"disambiguationData":[OSD([subQ8])]})}),makeQuery(id+"F6.opExtrude","SWEPT_FACE",FACE,{"disambiguationData":[OSD([sQuery(id+"F5.wireOp",EDGE,"E30")])]})]});}
            var Q25;
            {var subQ8=sQuery(id+"F1.wireOp",EDGE,"E12");var subQ10=sQuery(id+"F0.wireOp",EDGE,"E2.left");Q25=makeQuery(id+"F6.boolean.opBoolean","INTERSECT",EDGE,{"disambiguationData":[OD(0.0)],"derivedFrom":[makeQuery(id+"F3.boolean.opBoolean","SPLIT",FACE,{"disambiguationData":[TD([makeQuery(id+"F3.opExtrude","SWEPT_FACE",FACE,{"disambiguationData":[OSD([subQ10])]})])],"derivedFrom":makeQuery(id+"F2.opExtrude","SWEPT_FACE",FACE,{"disambiguationData":[OSD([subQ8])]})}),makeQuery(id+"F6.opExtrude","SWEPT_FACE",FACE,{"disambiguationData":[OSD([sQuery(id+"F5.wireOp",EDGE,"E25")])]})]});}
            var Q26;
            {var subQ8=sQuery(id+"F1.wireOp",EDGE,"E12");var subQ10=sQuery(id+"F0.wireOp",EDGE,"E2.right");Q26=makeQuery(id+"F6.boolean.opBoolean","INTERSECT",EDGE,{"disambiguationData":[OD(0.0)],"derivedFrom":[makeQuery(id+"F3.boolean.opBoolean","SPLIT",FACE,{"disambiguationData":[TD([makeQuery(id+"F3.opExtrude","SWEPT_FACE",FACE,{"disambiguationData":[OSD([subQ10])]})])],"derivedFrom":makeQuery(id+"F2.opExtrude","SWEPT_FACE",FACE,{"disambiguationData":[OSD([subQ8])]})}),makeQuery(id+"F6.opExtrude","SWEPT_FACE",FACE,{"disambiguationData":[OSD([sQuery(id+"F5.wireOp",EDGE,"E26")])]})]});}
            var Q27;
            {var subQ4=sQuery(id+"F0.wireOp",EDGE,"E3.right");var subQ8=sQuery(id+"F1.wireOp",EDGE,"E12");Q27=makeQuery(id+"F6.boolean.opBoolean","INTERSECT",EDGE,{"derivedFrom":[makeQuery(id+"F3.boolean.opBoolean","SPLIT",FACE,{"disambiguationData":[TD([makeQuery(id+"F3.opExtrude","SWEPT_FACE",FACE,{"disambiguationData":[OSD([subQ4])]})])],"derivedFrom":makeQuery(id+"F2.opExtrude","SWEPT_FACE",FACE,{"disambiguationData":[OSD([subQ8])]})}),makeQuery(id+"F6.opExtrude","SWEPT_FACE",FACE,{"disambiguationData":[OSD([sQuery(id+"F5.wireOp",EDGE,"E29")])]})]});}
            var Q28;
            {var subQ5=sQuery(id+"F0.wireOp",EDGE,"E3.left");var subQ8=sQuery(id+"F1.wireOp",EDGE,"E12");Q28=makeQuery(id+"F6.boolean.opBoolean","INTERSECT",EDGE,{"derivedFrom":[makeQuery(id+"F3.boolean.opBoolean","SPLIT",FACE,{"disambiguationData":[TD([makeQuery(id+"F3.opExtrude","SWEPT_FACE",FACE,{"disambiguationData":[OSD([subQ5])]})])],"derivedFrom":makeQuery(id+"F2.opExtrude","SWEPT_FACE",FACE,{"disambiguationData":[OSD([subQ8])]})}),makeQuery(id+"F6.opExtrude","SWEPT_FACE",FACE,{"disambiguationData":[OSD([sQuery(id+"F5.wireOp",EDGE,"E29")])]})]});}
            var Q29;
            {var subQ8=sQuery(id+"F1.wireOp",EDGE,"E12");var subQ10=sQuery(id+"F0.wireOp",EDGE,"E2.left");Q29=makeQuery(id+"F6.boolean.opBoolean","INTERSECT",EDGE,{"disambiguationData":[OD(1.0)],"derivedFrom":[makeQuery(id+"F3.boolean.opBoolean","SPLIT",FACE,{"disambiguationData":[TD([makeQuery(id+"F3.opExtrude","SWEPT_FACE",FACE,{"disambiguationData":[OSD([subQ10])]})])],"derivedFrom":makeQuery(id+"F2.opExtrude","SWEPT_FACE",FACE,{"disambiguationData":[OSD([subQ8])]})}),makeQuery(id+"F6.opExtrude","SWEPT_FACE",FACE,{"disambiguationData":[OSD([sQuery(id+"F5.wireOp",EDGE,"E25")])]})]});}
            var Q30;
            {var subQ8=sQuery(id+"F1.wireOp",EDGE,"E12");var subQ10=sQuery(id+"F0.wireOp",EDGE,"E2.right");Q30=makeQuery(id+"F6.boolean.opBoolean","INTERSECT",EDGE,{"disambiguationData":[OD(1.0)],"derivedFrom":[makeQuery(id+"F3.boolean.opBoolean","SPLIT",FACE,{"disambiguationData":[TD([makeQuery(id+"F3.opExtrude","SWEPT_FACE",FACE,{"disambiguationData":[OSD([subQ10])]})])],"derivedFrom":makeQuery(id+"F2.opExtrude","SWEPT_FACE",FACE,{"disambiguationData":[OSD([subQ8])]})}),makeQuery(id+"F6.opExtrude","SWEPT_FACE",FACE,{"disambiguationData":[OSD([sQuery(id+"F5.wireOp",EDGE,"E26")])]})]});}
            var Q31;
            {var subQ8=sQuery(id+"F1.wireOp",EDGE,"E12");var subQ12=sQuery(id+"F0.wireOp",EDGE,"E6.top");Q31=makeQuery(id+"F6.boolean.opBoolean","INTERSECT",EDGE,{"disambiguationData":[OD(0.0)],"derivedFrom":[makeQuery(id+"F3.boolean.opBoolean","SPLIT",FACE,{"disambiguationData":[TD([makeQuery(id+"F3.opExtrude","SWEPT_FACE",FACE,{"disambiguationData":[OSD([subQ12])]})])],"derivedFrom":makeQuery(id+"F2.opExtrude","SWEPT_FACE",FACE,{"disambiguationData":[OSD([subQ8])]})}),makeQuery(id+"F6.opExtrude","SWEPT_FACE",FACE,{"disambiguationData":[OSD([sQuery(id+"F5.wireOp",EDGE,"E27")])]})]});}
            var Q32;
            {var subQ8=sQuery(id+"F1.wireOp",EDGE,"E12");var subQ12=sQuery(id+"F0.wireOp",EDGE,"E6.top");Q32=makeQuery(id+"F6.boolean.opBoolean","INTERSECT",EDGE,{"disambiguationData":[OD(1.0)],"derivedFrom":[makeQuery(id+"F3.boolean.opBoolean","SPLIT",FACE,{"disambiguationData":[TD([makeQuery(id+"F3.opExtrude","SWEPT_FACE",FACE,{"disambiguationData":[OSD([subQ12])]})])],"derivedFrom":makeQuery(id+"F2.opExtrude","SWEPT_FACE",FACE,{"disambiguationData":[OSD([subQ8])]})}),makeQuery(id+"F6.opExtrude","SWEPT_FACE",FACE,{"disambiguationData":[OSD([sQuery(id+"F5.wireOp",EDGE,"E27")])]})]});}
            var Q33;
            {var subQ8=sQuery(id+"F1.wireOp",EDGE,"E12");var subQ12=sQuery(id+"F0.wireOp",EDGE,"E6.top");Q33=makeQuery(id+"F6.boolean.opBoolean","INTERSECT",EDGE,{"derivedFrom":[makeQuery(id+"F3.boolean.opBoolean","SPLIT",FACE,{"disambiguationData":[TD([makeQuery(id+"F3.opExtrude","SWEPT_FACE",FACE,{"disambiguationData":[OSD([subQ12])]})])],"derivedFrom":makeQuery(id+"F2.opExtrude","SWEPT_FACE",FACE,{"disambiguationData":[OSD([subQ8])]})}),makeQuery(id+"F6.opExtrude","SWEPT_FACE",FACE,{"disambiguationData":[OSD([sQuery(id+"F5.wireOp",EDGE,"E28")])]})]});}
            var Q34;
            {var subQ4=sQuery(id+"F0.wireOp",EDGE,"E3.right");var subQ8=sQuery(id+"F1.wireOp",EDGE,"E12");Q34=makeQuery(id+"F6.boolean.opBoolean","INTERSECT",EDGE,{"derivedFrom":[makeQuery(id+"F3.boolean.opBoolean","SPLIT",FACE,{"disambiguationData":[TD([makeQuery(id+"F3.opExtrude","SWEPT_FACE",FACE,{"disambiguationData":[OSD([subQ4])]})])],"derivedFrom":makeQuery(id+"F2.opExtrude","SWEPT_FACE",FACE,{"disambiguationData":[OSD([subQ8])]})}),makeQuery(id+"F6.opExtrude","SWEPT_FACE",FACE,{"disambiguationData":[OSD([sQuery(id+"F5.wireOp",EDGE,"E28")])]})]});}
            var Q35;
            {var subQ8=sQuery(id+"F1.wireOp",EDGE,"E12");var subQ10=sQuery(id+"F0.wireOp",EDGE,"E2.left");Q35=makeQuery(id+"F6.boolean.opBoolean","INTERSECT",EDGE,{"derivedFrom":[makeQuery(id+"F3.boolean.opBoolean","SPLIT",FACE,{"disambiguationData":[TD([makeQuery(id+"F3.opExtrude","SWEPT_FACE",FACE,{"disambiguationData":[OSD([subQ10])]})])],"derivedFrom":makeQuery(id+"F2.opExtrude","SWEPT_FACE",FACE,{"disambiguationData":[OSD([subQ8])]})}),makeQuery(id+"F6.opExtrude","SWEPT_FACE",FACE,{"disambiguationData":[OSD([sQuery(id+"F5.wireOp",EDGE,"E30")])]})]});}
            var Q36;
            Q36=makeQuery(id+"F6.boolean.opBoolean","INTERSECT",EDGE,{"derivedFrom":[makeQuery(id+"F3.opExtrude","SWEPT_FACE",FACE,{"disambiguationData":[OSD([sQuery(id+"F0.wireOp",EDGE,"E7.top")])]}),makeQuery(id+"F6.opExtrude","SWEPT_FACE",FACE,{"disambiguationData":[OSD([sQuery(id+"F5.wireOp",EDGE,"E30")])]})]});
            var Q37;
            Q37=makeQuery(id+"F6.boolean.opBoolean","INTERSECT",EDGE,{"derivedFrom":[makeQuery(id+"F3.opExtrude","SWEPT_FACE",FACE,{"disambiguationData":[OSD([sQuery(id+"F0.wireOp",EDGE,"E3.right")])]}),makeQuery(id+"F6.opExtrude","SWEPT_FACE",FACE,{"disambiguationData":[OSD([sQuery(id+"F5.wireOp",EDGE,"E29")])]})]});
            var Q38;
            Q38=makeQuery(id+"F6.boolean.opBoolean","INTERSECT",EDGE,{"derivedFrom":[makeQuery(id+"F3.opExtrude","SWEPT_FACE",FACE,{"disambiguationData":[OSD([sQuery(id+"F0.wireOp",EDGE,"E3.left")])]}),makeQuery(id+"F6.opExtrude","SWEPT_FACE",FACE,{"disambiguationData":[OSD([sQuery(id+"F5.wireOp",EDGE,"E29")])]})]});
            var Q39;
            Q39=makeQuery(id+"F6.boolean.opBoolean","INTERSECT",EDGE,{"derivedFrom":[makeQuery(id+"F3.opExtrude","SWEPT_FACE",FACE,{"disambiguationData":[OSD([sQuery(id+"F0.wireOp",EDGE,"E8.right")])]}),makeQuery(id+"F6.opExtrude","SWEPT_FACE",FACE,{"disambiguationData":[OSD([sQuery(id+"F5.wireOp",EDGE,"E28")])]})]});
            var Q40;
            Q40=makeQuery(id+"F6.boolean.opBoolean","INTERSECT",EDGE,{"derivedFrom":[makeQuery(id+"F3.opExtrude","SWEPT_FACE",FACE,{"disambiguationData":[OSD([sQuery(id+"F0.wireOp",EDGE,"E8.left")])]}),makeQuery(id+"F6.opExtrude","SWEPT_FACE",FACE,{"disambiguationData":[OSD([sQuery(id+"F5.wireOp",EDGE,"E28")])]})]});
            var Q41;
            Q41=makeQuery(id+"F6.boolean.opBoolean","INTERSECT",EDGE,{"derivedFrom":[makeQuery(id+"F3.opExtrude","SWEPT_FACE",FACE,{"disambiguationData":[OSD([sQuery(id+"F0.wireOp",EDGE,"E7.bottom")])]}),makeQuery(id+"F6.opExtrude","SWEPT_FACE",FACE,{"disambiguationData":[OSD([sQuery(id+"F5.wireOp",EDGE,"E30")])]})]});
            fillet(context, id + "F7", {"entities" : qUnion([Q0, Q1, Q2, Q3, Q4, Q5, Q6, Q7, Q8, Q9, Q10, Q11, Q12, Q13, Q14, Q15, Q16, Q17, Q18, Q19, Q20, Q21, Q22, Q23, Q24, Q25, Q26, Q27, Q28, Q29, Q30, Q31, Q32, Q33, Q34, Q35, Q36, Q37, Q38, Q39, Q40, Q41]), "radius" : 1 * mm, "tangentPropagation" : true, "allowEdgeOverflow" : false});
        }
        {
            var Q0;
            {var subQ0=sQuery(id+"F5.wireOp",EDGE,"E31");var subQ1=sQuery(id+"F5.wireOp",EDGE,"E13");var subQ2=makeQuery(id+"F5.imprint","INTERSECT",VERTEX,{"disambiguationData":[OD(0.0)],"derivedFrom":[subQ1,subQ0]});Q0=makeQuery(id+"F5.imprint","IMPRINT",FACE,{"disambiguationData":[TD([[makeQuery(id+"F5.imprint","IMPRINT",EDGE,{"disambiguationData":[TD([[subQ2,-1.0]])],"derivedFrom":subQ1}),-1.0]])]});}
            var Q1;
            {var subQ0=sQuery(id+"F5.wireOp",EDGE,"E31");var subQ1=sQuery(id+"F5.wireOp",EDGE,"E13");var subQ2=makeQuery(id+"F5.imprint","INTERSECT",VERTEX,{"disambiguationData":[OD(0.0)],"derivedFrom":[subQ1,subQ0]});Q1=makeQuery(id+"F5.imprint","IMPRINT",FACE,{"disambiguationData":[TD([[makeQuery(id+"F5.imprint","IMPRINT",EDGE,{"disambiguationData":[TD([[subQ2,-1.0]])],"derivedFrom":subQ1}),1.0]])]});}
            var Q2;
            {var subQ0=sQuery(id+"F5.wireOp",EDGE,"E32");var subQ1=sQuery(id+"F5.wireOp",EDGE,"E13");var subQ2=makeQuery(id+"F5.imprint","INTERSECT",VERTEX,{"disambiguationData":[OD(0.0)],"derivedFrom":[subQ1,subQ0]});Q2=makeQuery(id+"F5.imprint","IMPRINT",FACE,{"disambiguationData":[TD([[makeQuery(id+"F5.imprint","IMPRINT",EDGE,{"disambiguationData":[TD([[subQ2,-1.0]])],"derivedFrom":subQ1}),-1.0]])]});}
            var Q3;
            {var subQ0=sQuery(id+"F5.wireOp",EDGE,"E32");var subQ1=sQuery(id+"F5.wireOp",EDGE,"E13");var subQ2=makeQuery(id+"F5.imprint","INTERSECT",VERTEX,{"disambiguationData":[OD(0.0)],"derivedFrom":[subQ1,subQ0]});Q3=makeQuery(id+"F5.imprint","IMPRINT",FACE,{"disambiguationData":[TD([[makeQuery(id+"F5.imprint","IMPRINT",EDGE,{"disambiguationData":[TD([[subQ2,-1.0]])],"derivedFrom":subQ1}),1.0]])]});}
            var Q4;
            {var subQ0=sQuery(id+"F5.wireOp",EDGE,"E33");var subQ1=sQuery(id+"F5.wireOp",EDGE,"E13");var subQ2=makeQuery(id+"F5.imprint","INTERSECT",VERTEX,{"disambiguationData":[OD(0.0)],"derivedFrom":[subQ1,subQ0]});Q4=makeQuery(id+"F5.imprint","IMPRINT",FACE,{"disambiguationData":[TD([[makeQuery(id+"F5.imprint","IMPRINT",EDGE,{"disambiguationData":[TD([[subQ2,-1.0]])],"derivedFrom":subQ1}),1.0]])]});}
            var Q5;
            {var subQ0=sQuery(id+"F5.wireOp",EDGE,"E33");var subQ1=sQuery(id+"F5.wireOp",EDGE,"E13");var subQ2=makeQuery(id+"F5.imprint","INTERSECT",VERTEX,{"disambiguationData":[OD(0.0)],"derivedFrom":[subQ1,subQ0]});Q5=makeQuery(id+"F5.imprint","IMPRINT",FACE,{"disambiguationData":[TD([[makeQuery(id+"F5.imprint","IMPRINT",EDGE,{"disambiguationData":[TD([[subQ2,-1.0]])],"derivedFrom":subQ1}),-1.0]])]});}
            var Q6;
            {var subQ0=sQuery(id+"F5.wireOp",EDGE,"E34");var subQ1=sQuery(id+"F5.wireOp",EDGE,"E13");var subQ2=makeQuery(id+"F5.imprint","INTERSECT",VERTEX,{"disambiguationData":[OD(0.0)],"derivedFrom":[subQ1,subQ0]});Q6=makeQuery(id+"F5.imprint","IMPRINT",FACE,{"disambiguationData":[TD([[makeQuery(id+"F5.imprint","IMPRINT",EDGE,{"disambiguationData":[TD([[subQ2,-1.0]])],"derivedFrom":subQ1}),1.0]])]});}
            var Q7;
            {var subQ0=sQuery(id+"F5.wireOp",EDGE,"E34");var subQ1=sQuery(id+"F5.wireOp",EDGE,"E13");var subQ2=makeQuery(id+"F5.imprint","INTERSECT",VERTEX,{"disambiguationData":[OD(0.0)],"derivedFrom":[subQ1,subQ0]});Q7=makeQuery(id+"F5.imprint","IMPRINT",FACE,{"disambiguationData":[TD([[makeQuery(id+"F5.imprint","IMPRINT",EDGE,{"disambiguationData":[TD([[subQ2,-1.0]])],"derivedFrom":subQ1}),-1.0]])]});}
            var Q8;
            {var subQ1=sQuery(id+"F5.wireOp",EDGE,"E36.bottom");Q8=makeQuery(id+"F5.imprint","IMPRINT",FACE,{"disambiguationData":[TD([[makeQuery(id+"F5.imprint","IMPRINT",EDGE,{"derivedFrom":subQ1}),-1.0]])]});}
            var Q9;
            {var subQ0=sQuery(id+"F5.wireOp",EDGE,"E36.top");var subQ1=sQuery(id+"F5.wireOp",EDGE,"E13");var subQ2=makeQuery(id+"F5.imprint","INTERSECT",VERTEX,{"derivedFrom":[subQ1,subQ0]});Q9=makeQuery(id+"F5.imprint","IMPRINT",FACE,{"disambiguationData":[TD([[makeQuery(id+"F5.imprint","IMPRINT",EDGE,{"disambiguationData":[TD([[subQ2,-1.0]])],"derivedFrom":subQ1}),1.0]])]});}
            var Q10;
            {var subQ0=sQuery(id+"F5.wireOp",EDGE,"E35");var subQ1=sQuery(id+"F5.wireOp",EDGE,"E13");var subQ2=makeQuery(id+"F5.imprint","INTERSECT",VERTEX,{"disambiguationData":[OD(0.0)],"derivedFrom":[subQ1,subQ0]});Q10=makeQuery(id+"F5.imprint","IMPRINT",FACE,{"disambiguationData":[TD([[makeQuery(id+"F5.imprint","IMPRINT",EDGE,{"disambiguationData":[TD([[subQ2,-1.0]])],"derivedFrom":subQ1}),-1.0]])]});}
            var Q11;
            {var subQ0=sQuery(id+"F5.wireOp",EDGE,"E35");var subQ1=sQuery(id+"F5.wireOp",EDGE,"E13");var subQ2=makeQuery(id+"F5.imprint","INTERSECT",VERTEX,{"disambiguationData":[OD(0.0)],"derivedFrom":[subQ1,subQ0]});Q11=makeQuery(id+"F5.imprint","IMPRINT",FACE,{"disambiguationData":[TD([[makeQuery(id+"F5.imprint","IMPRINT",EDGE,{"disambiguationData":[TD([[subQ2,-1.0]])],"derivedFrom":subQ1}),1.0]])]});}
            extrude(context, id + "F8", {"entities" : qUnion([Q0, Q1, Q2, Q3, Q4, Q5, Q6, Q7, Q8, Q9, Q10, Q11]), "operationType" : NewBodyOperationType.ADD, "depth" : 11 * mm, "offsetDistance" : 25 * mm, "hasDraft" : true, "draftAngle" : 0.9 * degree, "draftPullDirection" : true});
        }
        {
            var Q0;
            Q0=qCreatedBy(makeId("Top.planeOp"),FACE);
            var sketch = newSketch(context, id + "F9", { "sketchPlane" : qUnion([Q0])});
            skCircle(sketch, "E37", {"center": v(0, 0) * mm, "radius": 4.1 * mm});
            skLineSegment(sketch, "E38", {"start": v(0, 0) * mm, "end": v(6.21, -23.18) * mm});
            skLineSegment(sketch, "E39.0", {"start": v(-1.93, -0.52) * mm, "end": v(4.8, -25.65) * mm});
            skLineSegment(sketch, "E40.0", {"start": v(1.93, 0.52) * mm, "end": v(8.6, -24.39) * mm});
            skCircle(sketch, "E41", {"center": v(-0.03, 0.11) * mm, "radius": 22.5 * mm});
            skSolve(sketch);
        }
        {
            var Q0;
            {var subQ0=sQuery(id+"F9.wireOp",EDGE,"E37");var subQ1=makeQuery(id+"F9.imprint","INTERSECT",VERTEX,{"derivedFrom":[subQ0,sQuery(id+"F9.wireOp",EDGE,"E39.0")]});Q0=makeQuery(id+"F9.imprint","IMPRINT",FACE,{"disambiguationData":[TD([[makeQuery(id+"F9.imprint","IMPRINT",EDGE,{"disambiguationData":[TD([[subQ1,-1.0]])],"derivedFrom":subQ0}),1.0]])]});}
            var Q1;
            {var subQ0=sQuery(id+"F9.wireOp",EDGE,"E39.0");var subQ1=sQuery(id+"F9.wireOp",EDGE,"E37");var subQ2=makeQuery(id+"F9.imprint","INTERSECT",VERTEX,{"derivedFrom":[subQ1,subQ0]});Q1=makeQuery(id+"F9.imprint","IMPRINT",FACE,{"disambiguationData":[TD([[makeQuery(id+"F9.imprint","IMPRINT",EDGE,{"disambiguationData":[TD([[subQ2,-1.0]])],"derivedFrom":subQ1}),-1.0]])]});}
            var Q2;
            {var subQ0=sQuery(id+"F9.wireOp",EDGE,"E40.0");var subQ1=sQuery(id+"F9.wireOp",EDGE,"E37");var subQ2=makeQuery(id+"F9.imprint","INTERSECT",VERTEX,{"derivedFrom":[subQ1,subQ0]});Q2=makeQuery(id+"F9.imprint","IMPRINT",FACE,{"disambiguationData":[TD([[makeQuery(id+"F9.imprint","IMPRINT",EDGE,{"disambiguationData":[TD([[subQ2,1.0]])],"derivedFrom":subQ1}),-1.0]])]});}
            var Q3;
            {var subQ0=sQuery(id+"F9.wireOp",EDGE,"E41");var subQ1=sQuery(id+"F9.wireOp",EDGE,"E38");var subQ2=makeQuery(id+"F9.imprint","INTERSECT",VERTEX,{"disambiguationData":[OD(0.0)],"derivedFrom":[subQ1,subQ0]});Q3=makeQuery(id+"F9.imprint","IMPRINT",FACE,{"disambiguationData":[TD([[makeQuery(id+"F9.imprint","IMPRINT",EDGE,{"disambiguationData":[TD([[subQ2,1.0]])],"derivedFrom":subQ1}),1.0]])]});}
            var Q4;
            {var subQ0=sQuery(id+"F9.wireOp",EDGE,"E41");var subQ1=sQuery(id+"F9.wireOp",EDGE,"E38");var subQ2=makeQuery(id+"F9.imprint","INTERSECT",VERTEX,{"disambiguationData":[OD(0.0)],"derivedFrom":[subQ1,subQ0]});Q4=makeQuery(id+"F9.imprint","IMPRINT",FACE,{"disambiguationData":[TD([[makeQuery(id+"F9.imprint","IMPRINT",EDGE,{"disambiguationData":[TD([[subQ2,1.0]])],"derivedFrom":subQ1}),-1.0]])]});}
            extrude(context, id + "F10", {"entities" : qUnion([Q0, Q1, Q2, Q3, Q4]), "operationType" : NewBodyOperationType.REMOVE, "depth" : 1 * mm, "offsetDistance" : 25 * mm});
        }
        {
            var Q0;
            {var subQ0=sQuery(id+"F1.wireOp",EDGE,"E11");var subQ1=sQuery(id+"F1.wireOp",EDGE,"E12");var subQ2=sQuery(id+"F0.wireOp",EDGE,"E10");var subQ3=sQuery(id+"F0.wireOp",EDGE,"E1.0");var subQ4=sQuery(id+"F5.wireOp",EDGE,"E27");var subQ5=sQuery(id+"F5.wireOp",EDGE,"E28");Q0=makeQuery(id+"F6.boolean.opBoolean","SPLIT",EDGE,{"disambiguationData":[TD([makeQuery(id+"F2.opExtrude","SWEPT_FACE",FACE,{"disambiguationData":[OSD([subQ0])]}),makeQuery(id+"F2.opExtrude","CAP_FACE",FACE,{"disambiguationData":[OSD([subQ0,subQ1])],"isStart":true}),makeQuery(id+"F3.opExtrude","CAP_FACE",FACE,{"disambiguationData":[OSD([subQ3,sQuery(id+"F0.wireOp",EDGE,"E2.left"),sQuery(id+"F0.wireOp",EDGE,"E2.right"),subQ2])],"isStart":true}),makeQuery(id+"F3.opExtrude","CAP_FACE",FACE,{"disambiguationData":[OSD([subQ3,sQuery(id+"F0.wireOp",EDGE,"E7.bottom"),sQuery(id+"F0.wireOp",EDGE,"E7.top"),subQ2])],"isStart":true}),makeQuery(id+"F3.opExtrude","CAP_FACE",FACE,{"disambiguationData":[OSD([subQ3,sQuery(id+"F0.wireOp",EDGE,"E3.left"),sQuery(id+"F0.wireOp",EDGE,"E3.right"),subQ2])],"isStart":true}),makeQuery(id+"F3.opExtrude","CAP_FACE",FACE,{"disambiguationData":[OSD([subQ3,sQuery(id+"F0.wireOp",EDGE,"E8.left"),sQuery(id+"F0.wireOp",EDGE,"E8.right"),subQ2])],"isStart":true}),makeQuery(id+"F3.opExtrude","CAP_FACE",FACE,{"disambiguationData":[OSD([subQ3,sQuery(id+"F0.wireOp",EDGE,"E6.bottom"),sQuery(id+"F0.wireOp",EDGE,"E6.top"),subQ2])],"isStart":true}),makeQuery(id+"F3.opExtrude","CAP_FACE",FACE,{"disambiguationData":[OSD([subQ0,subQ1])],"isStart":true}),makeQuery(id+"F4.opExtrude","CAP_FACE",FACE,{"disambiguationData":[OSD([subQ0])],"isStart":true}),makeQuery(id+"F6.opExtrude","CAP_FACE",FACE,{"disambiguationData":[OSD([sQuery(id+"F5.wireOp",EDGE,"E25")])],"isStart":true}),makeQuery(id+"F6.opExtrude","CAP_FACE",FACE,{"disambiguationData":[OSD([sQuery(id+"F5.wireOp",EDGE,"E26")])],"isStart":true}),makeQuery(id+"F6.opExtrude","SWEPT_FACE",FACE,{"disambiguationData":[OSD([subQ4])]}),makeQuery(id+"F6.opExtrude","CAP_FACE",FACE,{"disambiguationData":[OSD([subQ4])],"isStart":true}),makeQuery(id+"F6.opExtrude","SWEPT_FACE",FACE,{"disambiguationData":[OSD([subQ5])]}),makeQuery(id+"F6.opExtrude","CAP_FACE",FACE,{"disambiguationData":[OSD([subQ5])],"isStart":true}),makeQuery(id+"F6.opExtrude","CAP_FACE",FACE,{"disambiguationData":[OSD([sQuery(id+"F5.wireOp",EDGE,"E29")])],"isStart":true}),makeQuery(id+"F6.opExtrude","CAP_FACE",FACE,{"disambiguationData":[OSD([sQuery(id+"F5.wireOp",EDGE,"E30")])],"isStart":true})])],"derivedFrom":makeQuery(id+"F2.opExtrude","CAP_EDGE",EDGE,{"disambiguationData":[OSD([subQ0])],"isStart":true})});}
            var Q1;
            Q1=makeQuery(id+"F10.boolean.opBoolean","COPY",EDGE,{"derivedFrom":makeQuery(id+"F10.opExtrude","CAP_EDGE",EDGE,{"disambiguationData":[OSD([sQuery(id+"F9.wireOp",EDGE,"E40.0")])],"isStart":true})});
            var Q2;
            Q2=makeQuery(id+"F10.boolean.opBoolean","COPY",EDGE,{"derivedFrom":makeQuery(id+"F10.opExtrude","CAP_EDGE",EDGE,{"disambiguationData":[OSD([sQuery(id+"F9.wireOp",EDGE,"E40.0")])],"isStart":false})});
            var Q3;
            Q3=makeQuery(id+"F10.boolean.opBoolean","COPY",EDGE,{"derivedFrom":makeQuery(id+"F10.opExtrude","CAP_EDGE",EDGE,{"disambiguationData":[OSD([sQuery(id+"F9.wireOp",EDGE,"E37")])],"isStart":true})});
            var Q4;
            Q4=makeQuery(id+"F10.boolean.opBoolean","COPY",EDGE,{"derivedFrom":makeQuery(id+"F10.opExtrude","CAP_EDGE",EDGE,{"disambiguationData":[OSD([sQuery(id+"F9.wireOp",EDGE,"E37")])],"isStart":false})});
            var Q5;
            Q5=makeQuery(id+"F10.boolean.opBoolean","COPY",EDGE,{"derivedFrom":makeQuery(id+"F10.opExtrude","CAP_EDGE",EDGE,{"disambiguationData":[OSD([sQuery(id+"F9.wireOp",EDGE,"E39.0")])],"isStart":true})});
            var Q6;
            Q6=makeQuery(id+"F10.boolean.opBoolean","COPY",EDGE,{"derivedFrom":makeQuery(id+"F10.opExtrude","CAP_EDGE",EDGE,{"disambiguationData":[OSD([sQuery(id+"F9.wireOp",EDGE,"E41")])],"isStart":false})});
            var Q7;
            Q7=makeQuery(id+"F10.boolean.opBoolean","COPY",EDGE,{"derivedFrom":makeQuery(id+"F10.opExtrude","CAP_EDGE",EDGE,{"disambiguationData":[OSD([sQuery(id+"F9.wireOp",EDGE,"E41")])],"isStart":true})});
            var Q8;
            Q8=makeQuery(id+"F10.boolean.opBoolean","COPY",EDGE,{"derivedFrom":makeQuery(id+"F10.opExtrude","CAP_EDGE",EDGE,{"disambiguationData":[OSD([sQuery(id+"F9.wireOp",EDGE,"E39.0")])],"isStart":false})});
            fillet(context, id + "F11", {"entities" : qUnion([Q0, Q1, Q2, Q3, Q4, Q5, Q6, Q7, Q8]), "radius" : .5 * mm, "tangentPropagation" : true, "allowEdgeOverflow" : false});
        }
        {
            var Q0;
            Q0=makeQuery(id+"F8.opExtrude","CAP_EDGE",EDGE,{"disambiguationData":[OSD([sQuery(id+"F5.wireOp",EDGE,"E35")])],"isStart":false});
            var Q1;
            Q1=makeQuery(id+"F8.opExtrude","CAP_EDGE",EDGE,{"disambiguationData":[OSD([sQuery(id+"F5.wireOp",EDGE,"E31")])],"isStart":false});
            var Q2;
            Q2=makeQuery(id+"F8.opExtrude","CAP_EDGE",EDGE,{"disambiguationData":[OSD([sQuery(id+"F5.wireOp",EDGE,"E32")])],"isStart":false});
            var Q3;
            Q3=makeQuery(id+"F8.opExtrude","CAP_EDGE",EDGE,{"disambiguationData":[OSD([sQuery(id+"F5.wireOp",EDGE,"E33")])],"isStart":false});
            var Q4;
            Q4=makeQuery(id+"F8.opExtrude","CAP_EDGE",EDGE,{"disambiguationData":[OSD([sQuery(id+"F5.wireOp",EDGE,"E34")])],"isStart":false});
            var Q5;
            Q5=makeQuery(id+"F8.opExtrude","CAP_EDGE",EDGE,{"disambiguationData":[OSD([sQuery(id+"F5.wireOp",EDGE,"E36.bottom")])],"isStart":false});
            var Q6;
            Q6=makeQuery(id+"F8.opExtrude","CAP_EDGE",EDGE,{"disambiguationData":[OSD([sQuery(id+"F5.wireOp",EDGE,"E36.left")])],"isStart":false});
            var Q7;
            Q7=makeQuery(id+"F8.opExtrude","CAP_EDGE",EDGE,{"disambiguationData":[OSD([sQuery(id+"F5.wireOp",EDGE,"E36.top")])],"isStart":false});
            var Q8;
            Q8=makeQuery(id+"F8.opExtrude","CAP_EDGE",EDGE,{"disambiguationData":[OSD([sQuery(id+"F5.wireOp",EDGE,"E36.right")])],"isStart":false});
            fillet(context, id + "F12", {"entities" : qUnion([Q0, Q1, Q2, Q3, Q4, Q5, Q6, Q7, Q8]), "radius" : .45 * mm, "tangentPropagation" : true, "allowEdgeOverflow" : false});
        }
    });
